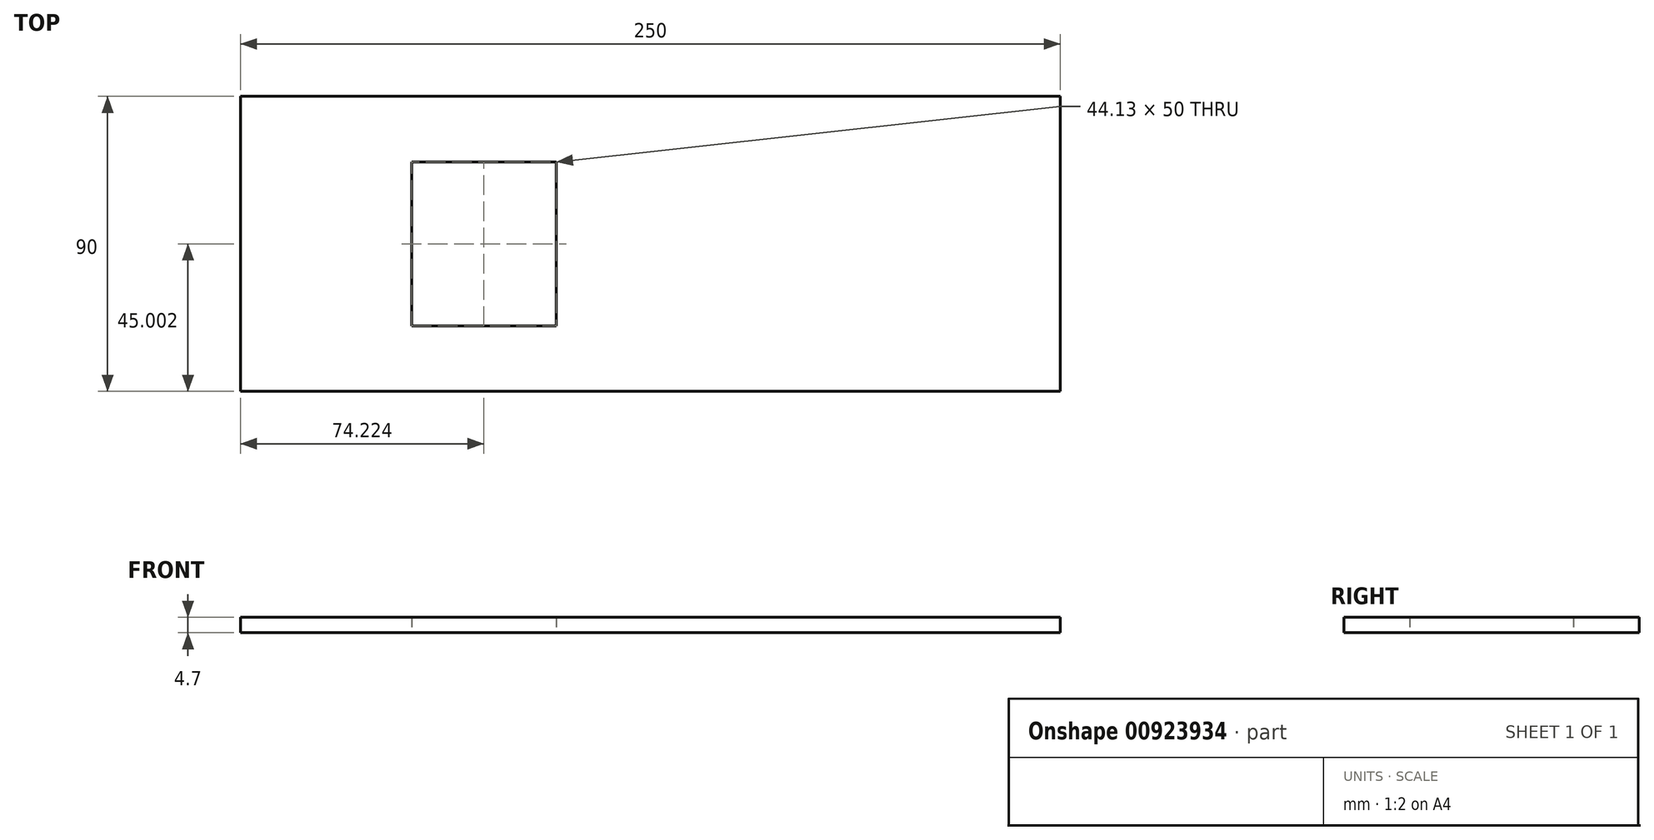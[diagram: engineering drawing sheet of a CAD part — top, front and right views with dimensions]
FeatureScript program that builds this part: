
annotation { "Feature Type Name" : "Feature", "Feature Type Description" : "" }
export const myFeature = defineFeature(function(context is Context, id is Id, definition is map)
    precondition{}
    {
        {
            var Q0;
            Q0=qCreatedBy(makeId("Top.planeOp"),FACE);
            var sketch = newSketch(context, id + "F0", { "sketchPlane" : qUnion([Q0])});
            skLineSegment(sketch, "E0.bottom", {"start": v(-124.07, 43.75) * mm, "end": v(125.93, 43.75) * mm});
            skLineSegment(sketch, "E0.top", {"start": v(-124.07, -46.25) * mm, "end": v(125.93, -46.25) * mm});
            skLineSegment(sketch, "E0.left", {"start": v(-124.07, 43.75) * mm, "end": v(-124.07, -46.25) * mm});
            skLineSegment(sketch, "E0.right", {"start": v(125.93, 43.75) * mm, "end": v(125.93, -46.25) * mm});
            skLineSegment(sketch, "E1", {"start": v(-71.91, 23.75) * mm, "end": v(-71.91, -26.25) * mm});
            skLineSegment(sketch, "E2", {"start": v(-71.91, -26.25) * mm, "end": v(-27.78, -26.25) * mm});
            skLineSegment(sketch, "E3", {"start": v(-27.78, -26.25) * mm, "end": v(-27.78, 23.75) * mm});
            skLineSegment(sketch, "E4", {"start": v(-27.78, 23.75) * mm, "end": v(-71.91, 23.75) * mm});
            skSolve(sketch);
        }
        {
            var Q0;
            Q0=makeQuery(id+"F0.imprint","IMPRINT",FACE,{"disambiguationData":[TD([[makeQuery(id+"F0.imprint","IMPRINT",EDGE,{"derivedFrom":sQuery(id+"F0.wireOp",EDGE,"E0.bottom")}),-1.0]])]});
            extrude(context, id + "F1", {"entities" : qUnion([Q0]), "depth" : 4.7 * mm, "offsetDistance" : 25 * mm});
        }
    });
